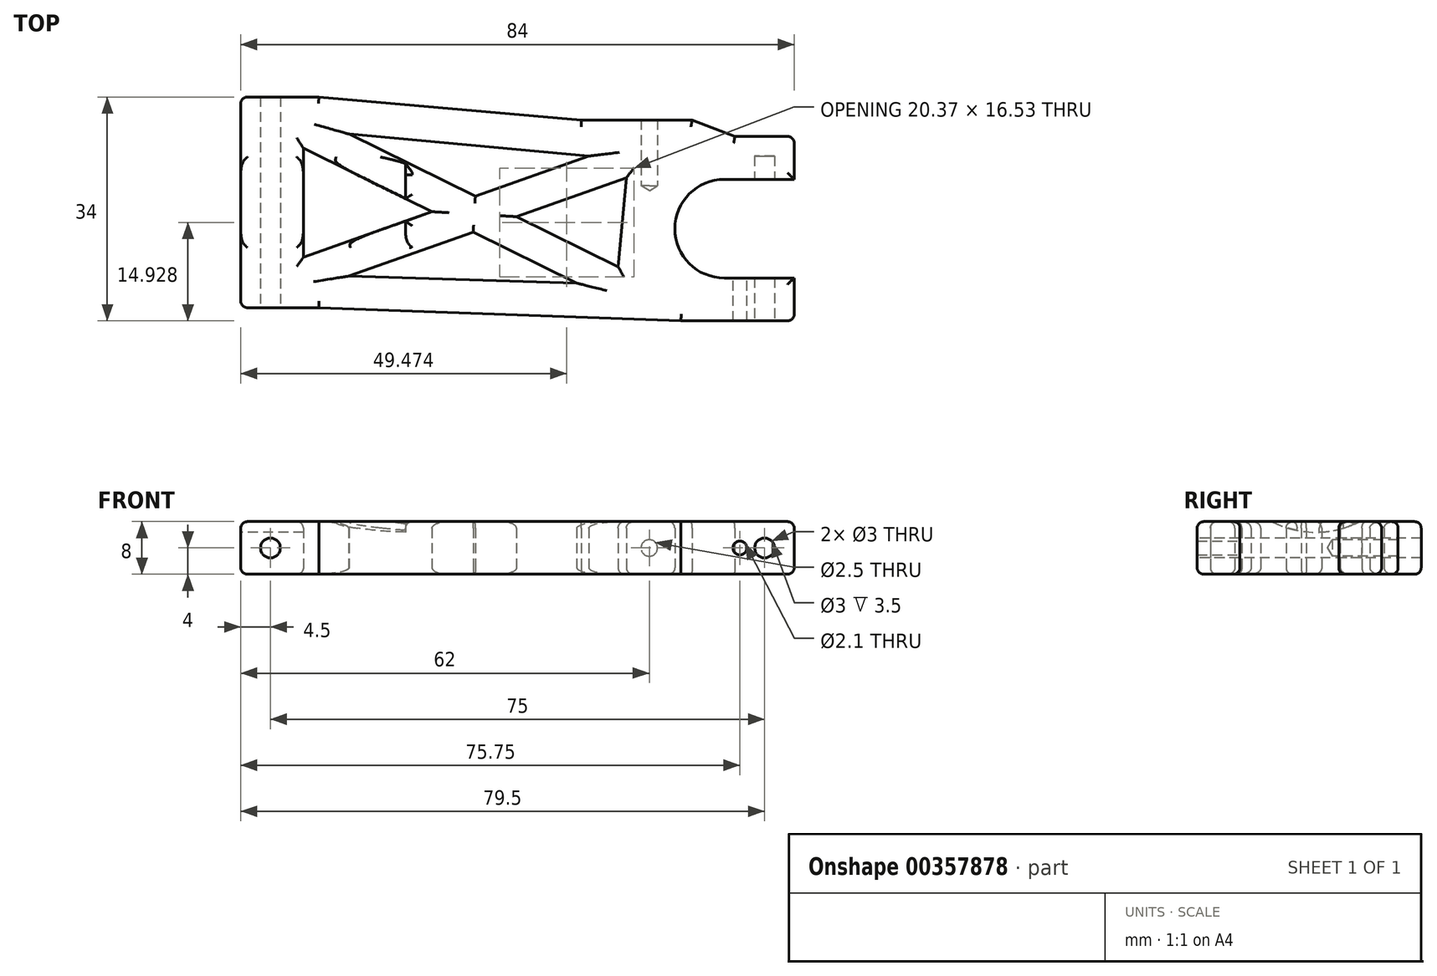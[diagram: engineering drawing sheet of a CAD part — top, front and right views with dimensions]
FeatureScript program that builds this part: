
annotation { "Feature Type Name" : "Feature", "Feature Type Description" : "" }
export const myFeature = defineFeature(function(context is Context, id is Id, definition is map)
    precondition{}
    {
        {
            var Q0;
            Q0=qCreatedBy(makeId("Top.planeOp"),FACE);
            var sketch = newSketch(context, id + "F0", { "sketchPlane" : qUnion([Q0])});
            skLineSegment(sketch, "E0", {"start": v(-37.5, 44.88) * mm, "end": v(-37.5, -3.08) * mm, "construction": true});
            skLineSegment(sketch, "E1", {"start": v(37.5, 44.88) * mm, "end": v(37.5, -31.83) * mm, "construction": true});
            skLineSegment(sketch, "E2", {"start": v(31.4, 0) * mm, "end": v(40.56, 0) * mm, "construction": true});
            skLineSegment(sketch, "E3", {"start": v(-41.87, 2) * mm, "end": v(-33.77, 2) * mm, "construction": true});
            skLineSegment(sketch, "E4", {"start": v(41.9, 28) * mm, "end": v(31.11, 28) * mm, "construction": true});
            skLineSegment(sketch, "E5", {"start": v(-40.76, 34) * mm, "end": v(-34.39, 34) * mm, "construction": true});
            skLineSegment(sketch, "E6", {"start": v(33.75, 2.56) * mm, "end": v(33.75, -2.35) * mm, "construction": true});
            skLineSegment(sketch, "E7", {"start": v(40.8, 30.5) * mm, "end": v(17.25, 30.5) * mm, "construction": true});
            skLineSegment(sketch, "E8", {"start": v(20, 32.37) * mm, "end": v(20, 27.7) * mm, "construction": true});
            skPoint(sketch, "E9", {"position": v(-37.5, 34) * mm});
            skPoint(sketch, "E10", {"position": v(-37.5, 2) * mm});
            skPoint(sketch, "E11", {"position": v(33.75, 0) * mm});
            skPoint(sketch, "E12", {"position": v(37.5, 0) * mm});
            skPoint(sketch, "E13", {"position": v(37.5, 28) * mm});
            skPoint(sketch, "E14", {"position": v(20, 30.5) * mm});
            skSolve(sketch);
        }
        {
            var Q0;
            Q0=qCreatedBy(makeId("Top.planeOp"),FACE);
            var sketch = newSketch(context, id + "F1", { "sketchPlane" : qUnion([Q0])});
            skLineSegment(sketch, "E15", {"start": v(-42, 34) * mm, "end": v(-42, 2) * mm});
            skLineSegment(sketch, "E16", {"start": v(-42, 2) * mm, "end": v(-30.15, 2) * mm});
            skLineSegment(sketch, "E17", {"start": v(-30.15, 2) * mm, "end": v(24.82, 0) * mm});
            skLineSegment(sketch, "E18", {"start": v(24.82, 0) * mm, "end": v(42, 0) * mm});
            skLineSegment(sketch, "E19", {"start": v(42, 0) * mm, "end": v(42, 28) * mm});
            skLineSegment(sketch, "E20", {"start": v(26.51, 30.5) * mm, "end": v(9.7, 30.5) * mm});
            skLineSegment(sketch, "E21", {"start": v(9.7, 30.5) * mm, "end": v(-30.15, 34) * mm});
            skLineSegment(sketch, "E22", {"start": v(-42, 34) * mm, "end": v(-30.15, 34) * mm});
            skLineSegment(sketch, "E23", {"start": v(42, 28) * mm, "end": v(33, 28) * mm});
            skLineSegment(sketch, "E24", {"start": v(33, 28) * mm, "end": v(26.51, 30.5) * mm});
            skLineSegment(sketch, "E25", {"start": v(-32.5, 29) * mm, "end": v(-32.5, 7) * mm});
            skLineSegment(sketch, "E26", {"start": v(32.5, 23.03) * mm, "end": v(32.5, 5) * mm});
            skLineSegment(sketch, "E27", {"start": v(-32.5, 29) * mm, "end": v(32.5, 23.03) * mm});
            skLineSegment(sketch, "E28", {"start": v(-32.5, 7) * mm, "end": v(32.5, 5) * mm});
            skPoint(sketch, "E29.startSnap0", {"position": v(-2.67, 1) * mm});
            skLineSegment(sketch, "E30", {"start": v(0, 6) * mm, "end": v(0, 26.01) * mm, "construction": true});
            skLineSegment(sketch, "E31", {"start": v(-32.5, 29) * mm, "end": v(15.03, 5.54) * mm, "construction": true});
            skLineSegment(sketch, "E32", {"start": v(-32.5, 7) * mm, "end": v(16.77, 24.47) * mm, "construction": true});
            skLineSegment(sketch, "E33", {"start": v(-6.56, 16.2) * mm, "end": v(15.37, 15.06) * mm, "construction": true});
            skLineSegment(sketch, "E34", {"start": v(15.37, 15.06) * mm, "end": v(32.5, 14.01) * mm, "construction": true});
            skLineSegment(sketch, "E35", {"start": v(-6.56, 16.2) * mm, "end": v(-32.5, 18) * mm, "construction": true});
            skLineSegment(sketch, "E36", {"start": v(-32.5, 26.21) * mm, "end": v(9.01, 5.72) * mm});
            skLineSegment(sketch, "E37", {"start": v(-25.56, 28.36) * mm, "end": v(21.06, 5.35) * mm});
            skLineSegment(sketch, "E38", {"start": v(-32.5, 9.65) * mm, "end": v(10.83, 25.02) * mm});
            skLineSegment(sketch, "E39", {"start": v(-25.62, 6.79) * mm, "end": v(22.72, 23.92) * mm});
            skPoint(sketch, "E40", {"position": v(42, 6.5) * mm});
            skPoint(sketch, "E41", {"position": v(42, 21.5) * mm});
            skLineSegment(sketch, "E42", {"start": v(42, 21.5) * mm, "end": v(31.38, 21.5) * mm});
            skLineSegment(sketch, "E43", {"start": v(42, 6.5) * mm, "end": v(31.38, 6.5) * mm});
            skArc(sketch, "E44", {"start": v(31.38, 21.5) * mm, "mid": v(23.88, 14) * mm, "end": v(31.38, 6.5) * mm});
            skLineSegment(sketch, "E45", {"start": v(15.03, 5.54) * mm, "end": v(16.77, 24.47) * mm});
            skSolve(sketch);
        }
        {
            var Q0;
            Q0=makeQuery(id+"F1.imprint","IMPRINT",FACE,{"disambiguationData":[TD([[makeQuery(id+"F1.imprint","IMPRINT",EDGE,{"derivedFrom":sQuery(id+"F1.wireOp",EDGE,"E15")}),1.0]])]});
            var Q1;
            {var subQ1=sQuery(id+"F1.wireOp",EDGE,"E27");var subQ6=sQuery(id+"F1.wireOp",EDGE,"E25");var subQ9=makeQuery(id+"F1.imprint","INTERSECT",VERTEX,{"derivedFrom":[subQ6,subQ1]});Q1=makeQuery(id+"F1.imprint","IMPRINT",FACE,{"disambiguationData":[TD([[makeQuery(id+"F1.imprint","IMPRINT",EDGE,{"disambiguationData":[TD([[subQ9,-1.0]])],"derivedFrom":subQ6}),1.0]])]});}
            var Q2;
            {var subQ0=sQuery(id+"F1.wireOp",EDGE,"E38");var subQ1=sQuery(id+"F1.wireOp",EDGE,"E36");var subQ2=makeQuery(id+"F1.imprint","INTERSECT",VERTEX,{"derivedFrom":[subQ1,subQ0]});Q2=makeQuery(id+"F1.imprint","IMPRINT",FACE,{"disambiguationData":[TD([[makeQuery(id+"F1.imprint","IMPRINT",EDGE,{"disambiguationData":[TD([[subQ2,-1.0]])],"derivedFrom":subQ1}),1.0]])]});}
            var Q3;
            {var subQ0=sQuery(id+"F1.wireOp",EDGE,"E38");var subQ1=sQuery(id+"F1.wireOp",EDGE,"E27");var subQ2=makeQuery(id+"F1.imprint","INTERSECT",VERTEX,{"derivedFrom":[subQ1,subQ0]});Q3=makeQuery(id+"F1.imprint","IMPRINT",FACE,{"disambiguationData":[TD([[makeQuery(id+"F1.imprint","IMPRINT",EDGE,{"disambiguationData":[TD([[subQ2,-1.0]])],"derivedFrom":subQ1}),-1.0]])]});}
            var Q4;
            {var subQ0=sQuery(id+"F1.wireOp",EDGE,"E39");var subQ1=sQuery(id+"F1.wireOp",EDGE,"E27");var subQ2=makeQuery(id+"F1.imprint","INTERSECT",VERTEX,{"derivedFrom":[subQ1,subQ0]});Q4=makeQuery(id+"F1.imprint","IMPRINT",FACE,{"disambiguationData":[TD([[makeQuery(id+"F1.imprint","IMPRINT",EDGE,{"disambiguationData":[TD([[subQ2,1.0]])],"derivedFrom":subQ1}),-1.0]])]});}
            var Q5;
            {var subQ16=sQuery(id+"F1.wireOp",EDGE,"E44");Q5=makeQuery(id+"F1.imprint","IMPRINT",FACE,{"disambiguationData":[TD([[makeQuery(id+"F1.imprint","IMPRINT",EDGE,{"derivedFrom":subQ16}),-1.0]])]});}
            var Q6;
            {var subQ0=sQuery(id+"F1.wireOp",EDGE,"E37");var subQ1=sQuery(id+"F1.wireOp",EDGE,"E28");var subQ2=makeQuery(id+"F1.imprint","INTERSECT",VERTEX,{"derivedFrom":[subQ1,subQ0]});Q6=makeQuery(id+"F1.imprint","IMPRINT",FACE,{"disambiguationData":[TD([[makeQuery(id+"F1.imprint","IMPRINT",EDGE,{"disambiguationData":[TD([[subQ2,1.0]])],"derivedFrom":subQ1}),1.0]])]});}
            var Q7;
            {var subQ1=sQuery(id+"F1.wireOp",EDGE,"E36");var subQ7=sQuery(id+"F1.wireOp",EDGE,"E28");var subQ8=makeQuery(id+"F1.imprint","INTERSECT",VERTEX,{"derivedFrom":[subQ7,subQ1]});Q7=makeQuery(id+"F1.imprint","IMPRINT",FACE,{"disambiguationData":[TD([[makeQuery(id+"F1.imprint","IMPRINT",EDGE,{"disambiguationData":[TD([[subQ8,-1.0]])],"derivedFrom":subQ7}),1.0]])]});}
            var Q8;
            {var subQ1=sQuery(id+"F1.wireOp",EDGE,"E25");var subQ5=sQuery(id+"F1.wireOp",EDGE,"E28");var subQ6=makeQuery(id+"F1.imprint","INTERSECT",VERTEX,{"derivedFrom":[subQ1,subQ5]});Q8=makeQuery(id+"F1.imprint","IMPRINT",FACE,{"disambiguationData":[TD([[makeQuery(id+"F1.imprint","IMPRINT",EDGE,{"disambiguationData":[TD([[subQ6,1.0]])],"derivedFrom":subQ1}),1.0]])]});}
            extrude(context, id + "F2", {"entities" : qUnion([Q0, Q1, Q2, Q3, Q4, Q5, Q6, Q7, Q8]), "depth" : 4 * mm});
        }
        {
            var Q0;
            Q0=makeQuery(id+"F2.opExtrude","CAP_FACE",FACE,{"disambiguationData":[OSD([sQuery(id+"F1.wireOp",EDGE,"E15"),sQuery(id+"F1.wireOp",EDGE,"E16"),sQuery(id+"F1.wireOp",EDGE,"E17"),sQuery(id+"F1.wireOp",EDGE,"E18"),sQuery(id+"F1.wireOp",EDGE,"E19"),sQuery(id+"F1.wireOp",EDGE,"E20"),sQuery(id+"F1.wireOp",EDGE,"E21"),sQuery(id+"F1.wireOp",EDGE,"E22"),sQuery(id+"F1.wireOp",EDGE,"E23"),sQuery(id+"F1.wireOp",EDGE,"E24"),sQuery(id+"F1.wireOp",EDGE,"E25"),sQuery(id+"F1.wireOp",EDGE,"E27"),sQuery(id+"F1.wireOp",EDGE,"E28"),sQuery(id+"F1.wireOp",EDGE,"E36"),sQuery(id+"F1.wireOp",EDGE,"E37"),sQuery(id+"F1.wireOp",EDGE,"E38"),sQuery(id+"F1.wireOp",EDGE,"E39"),sQuery(id+"F1.wireOp",EDGE,"E42"),sQuery(id+"F1.wireOp",EDGE,"E43"),sQuery(id+"F1.wireOp",EDGE,"E44"),sQuery(id+"F1.wireOp",EDGE,"E45")])],"isStart":true});
            extrude(context, id + "F3", {"entities" : qUnion([Q0]), "operationType" : NewBodyOperationType.ADD, "depth" : 4 * mm});
        }
        {
            var Q0;
            Q0=makeQuery(id+"F2.opExtrude","SWEPT_FACE",FACE,{"disambiguationData":[OSD([sQuery(id+"F1.wireOp",EDGE,"E22")])]});
            var sketch = newSketch(context, id + "F4", { "sketchPlane" : qUnion([Q0])});
            skPoint(sketch, "E46", {"position": v(37.5, 0) * mm});
            skSolve(sketch);
        }
        {
            var Q0;
            Q0=makeQuery(id+"F2.opExtrude","SWEPT_FACE",FACE,{"disambiguationData":[OSD([sQuery(id+"F1.wireOp",EDGE,"E18")])]});
            var sketch = newSketch(context, id + "F5", { "sketchPlane" : qUnion([Q0])});
            skPoint(sketch, "E47", {"position": v(33.75, 0) * mm});
            skPoint(sketch, "E48", {"position": v(37.5, 0) * mm});
            skCircle(sketch, "E49", {"center": v(37.5, 0) * mm, "radius": 1.5 * mm});
            skSolve(sketch);
        }
        {
            var Q0;
            Q0=sQuery(id+"F4.wireOp",VERTEX,"E46");
            var Q1;
            Q1=makeQuery(id+"F2.opExtrude","SWEPT_BODY",BODY,{"disambiguationData":[OSD([sQuery(id+"F1.wireOp",EDGE,"E15"),sQuery(id+"F1.wireOp",EDGE,"E16"),sQuery(id+"F1.wireOp",EDGE,"E17"),sQuery(id+"F1.wireOp",EDGE,"E18"),sQuery(id+"F1.wireOp",EDGE,"E19"),sQuery(id+"F1.wireOp",EDGE,"E20"),sQuery(id+"F1.wireOp",EDGE,"E21"),sQuery(id+"F1.wireOp",EDGE,"E22"),sQuery(id+"F1.wireOp",EDGE,"E23"),sQuery(id+"F1.wireOp",EDGE,"E24")])]});
            hole(context, id + "F6", {"style" : HoleStyle.SIMPLE, "endStyle" : HoleEndStyle.BLIND, "holeDiameter" : 3 * mm, "holeDepth" : 40 * mm, "isTappedThrough" : true, "tappedDepth" : 12 * mm, "tapClearance" : 3, "locations" : qUnion([Q0]), "scope" : qUnion([Q1])});
        }
        {
            var Q0;
            Q0=makeQuery(id+"F2.opExtrude","SWEPT_FACE",FACE,{"disambiguationData":[OSD([sQuery(id+"F1.wireOp",EDGE,"E20")])]});
            var sketch = newSketch(context, id + "F7", { "sketchPlane" : qUnion([Q0])});
            skPoint(sketch, "E50", {"position": v(-20, 0) * mm});
            skSolve(sketch);
        }
        {
            var Q0;
            Q0=sQuery(id+"F7.wireOp",VERTEX,"E50");
            var Q1;
            Q1=makeQuery(id+"F2.opExtrude","SWEPT_BODY",BODY,{"disambiguationData":[OSD([sQuery(id+"F1.wireOp",EDGE,"E15"),sQuery(id+"F1.wireOp",EDGE,"E16"),sQuery(id+"F1.wireOp",EDGE,"E17"),sQuery(id+"F1.wireOp",EDGE,"E18"),sQuery(id+"F1.wireOp",EDGE,"E19"),sQuery(id+"F1.wireOp",EDGE,"E20"),sQuery(id+"F1.wireOp",EDGE,"E21"),sQuery(id+"F1.wireOp",EDGE,"E22"),sQuery(id+"F1.wireOp",EDGE,"E23"),sQuery(id+"F1.wireOp",EDGE,"E24")])]});
            hole(context, id + "F8", {"style" : HoleStyle.SIMPLE, "endStyle" : HoleEndStyle.BLIND, "holeDiameter" : 2.5 * mm, "holeDepth" : 10 * mm, "isTappedThrough" : true, "tappedDepth" : 12 * mm, "tapClearance" : 3, "locations" : qUnion([Q0]), "scope" : qUnion([Q1])});
        }
        {
            var Q0;
            Q0=makeQuery(id+"F5.imprint","IMPRINT",FACE,{"disambiguationData":[TD([[makeQuery(id+"F5.imprint","IMPRINT",EDGE,{"derivedFrom":sQuery(id+"F5.wireOp",EDGE,"E49")}),1.0]])]});
            extrude(context, id + "F9", {"entities" : qUnion([Q0]), "operationType" : NewBodyOperationType.REMOVE, "oppositeDirection" : true, "depth" : 25 * mm});
        }
        {
            var Q0;
            {var subQ0=sQuery(id+"F1.wireOp",EDGE,"E15");Q0=makeQuery(id+"F3.boolean.opBoolean","MERGE",FACE,{"derivedFrom":[makeQuery(id+"F2.opExtrude","SWEPT_FACE",FACE,{"disambiguationData":[OSD([subQ0])]}),makeQuery(id+"F3.opExtrude","SWEPT_FACE",FACE,{"disambiguationData":[OSD([subQ0])]})]});}
            var sketch = newSketch(context, id + "F10", { "sketchPlane" : qUnion([Q0])});
            skArc(sketch, "E51", {"start": v(-24.65, 4) * mm, "mid": v(-18, 2.4) * mm, "end": v(-11.35, 4) * mm});
            skSolve(sketch);
        }
        {
            var Q0;
            {var subQ0=sQuery(id+"F10.wireOp",EDGE,"E51");Q0=makeQuery(id+"F10.imprint","IMPRINT",FACE,{"disambiguationData":[TD([[makeQuery(id+"F10.imprint","IMPRINT",EDGE,{"derivedFrom":subQ0}),1.0]])]});}
            extrude(context, id + "F11", {"entities" : qUnion([Q0]), "operationType" : NewBodyOperationType.REMOVE, "oppositeDirection" : true, "depth" : 25 * mm});
        }
        {
            var Q0;
            Q0=sQuery(id+"F5.wireOp",VERTEX,"E47");
            var Q1;
            Q1=makeQuery(id+"F2.opExtrude","SWEPT_BODY",BODY,{"disambiguationData":[OSD([sQuery(id+"F1.wireOp",EDGE,"E15"),sQuery(id+"F1.wireOp",EDGE,"E16"),sQuery(id+"F1.wireOp",EDGE,"E17"),sQuery(id+"F1.wireOp",EDGE,"E18"),sQuery(id+"F1.wireOp",EDGE,"E19"),sQuery(id+"F1.wireOp",EDGE,"E20"),sQuery(id+"F1.wireOp",EDGE,"E21"),sQuery(id+"F1.wireOp",EDGE,"E22"),sQuery(id+"F1.wireOp",EDGE,"E23"),sQuery(id+"F1.wireOp",EDGE,"E24")])]});
            hole(context, id + "F12", {"style" : HoleStyle.SIMPLE, "endStyle" : HoleEndStyle.BLIND, "holeDiameter" : 2.1 * mm, "holeDepth" : 10 * mm, "isTappedThrough" : true, "tappedDepth" : 12 * mm, "tapClearance" : 3, "locations" : qUnion([Q0]), "scope" : qUnion([Q1])});
        }
        {
            var Q0;
            Q0=makeQuery(id+"F3.opExtrude","CAP_FACE",FACE,{"disambiguationData":[OSD([sQuery(id+"F1.wireOp",EDGE,"E15"),sQuery(id+"F1.wireOp",EDGE,"E16"),sQuery(id+"F1.wireOp",EDGE,"E17"),sQuery(id+"F1.wireOp",EDGE,"E18"),sQuery(id+"F1.wireOp",EDGE,"E19"),sQuery(id+"F1.wireOp",EDGE,"E20"),sQuery(id+"F1.wireOp",EDGE,"E21"),sQuery(id+"F1.wireOp",EDGE,"E22"),sQuery(id+"F1.wireOp",EDGE,"E23"),sQuery(id+"F1.wireOp",EDGE,"E24"),sQuery(id+"F1.wireOp",EDGE,"E25"),sQuery(id+"F1.wireOp",EDGE,"E27"),sQuery(id+"F1.wireOp",EDGE,"E28"),sQuery(id+"F1.wireOp",EDGE,"E36"),sQuery(id+"F1.wireOp",EDGE,"E37"),sQuery(id+"F1.wireOp",EDGE,"E38"),sQuery(id+"F1.wireOp",EDGE,"E39"),sQuery(id+"F1.wireOp",EDGE,"E42"),sQuery(id+"F1.wireOp",EDGE,"E43"),sQuery(id+"F1.wireOp",EDGE,"E44"),sQuery(id+"F1.wireOp",EDGE,"E45")])],"isStart":false});
            var Q1;
            Q1=makeQuery(id+"F2.opExtrude","CAP_FACE",FACE,{"disambiguationData":[OSD([sQuery(id+"F1.wireOp",EDGE,"E15"),sQuery(id+"F1.wireOp",EDGE,"E16"),sQuery(id+"F1.wireOp",EDGE,"E17"),sQuery(id+"F1.wireOp",EDGE,"E18"),sQuery(id+"F1.wireOp",EDGE,"E19"),sQuery(id+"F1.wireOp",EDGE,"E20"),sQuery(id+"F1.wireOp",EDGE,"E21"),sQuery(id+"F1.wireOp",EDGE,"E22"),sQuery(id+"F1.wireOp",EDGE,"E23"),sQuery(id+"F1.wireOp",EDGE,"E24"),sQuery(id+"F1.wireOp",EDGE,"E25"),sQuery(id+"F1.wireOp",EDGE,"E27"),sQuery(id+"F1.wireOp",EDGE,"E28"),sQuery(id+"F1.wireOp",EDGE,"E36"),sQuery(id+"F1.wireOp",EDGE,"E37"),sQuery(id+"F1.wireOp",EDGE,"E38"),sQuery(id+"F1.wireOp",EDGE,"E39"),sQuery(id+"F1.wireOp",EDGE,"E42"),sQuery(id+"F1.wireOp",EDGE,"E43"),sQuery(id+"F1.wireOp",EDGE,"E44"),sQuery(id+"F1.wireOp",EDGE,"E45")])],"isStart":false});
            fillet(context, id + "F13", {"entities" : qUnion([Q0, Q1]), "radius" : 1 * mm, "tangentPropagation" : true, "allowEdgeOverflow" : false});
        }
        {
            var Q0;
            Q0=makeQuery(id+"F2.opExtrude","SWEPT_EDGE",EDGE,{"disambiguationData":[OSD([sQuery(id+"F1.wireOp",EDGE,"E15"),sQuery(id+"F1.wireOp",EDGE,"E16")])]});
            var Q1;
            Q1=makeQuery(id+"F2.opExtrude","SWEPT_EDGE",EDGE,{"disambiguationData":[OSD([sQuery(id+"F1.wireOp",EDGE,"E15"),sQuery(id+"F1.wireOp",EDGE,"E22")])]});
            var Q2;
            Q2=makeQuery(id+"F2.opExtrude","SWEPT_EDGE",EDGE,{"disambiguationData":[OSD([sQuery(id+"F1.wireOp",EDGE,"E18"),sQuery(id+"F1.wireOp",EDGE,"E19")])]});
            var Q3;
            Q3=makeQuery(id+"F2.opExtrude","SWEPT_EDGE",EDGE,{"disambiguationData":[OSD([sQuery(id+"F1.wireOp",EDGE,"E19"),sQuery(id+"F1.wireOp",EDGE,"E23")])]});
            fillet(context, id + "F14", {"entities" : qUnion([Q0, Q1, Q2, Q3]), "radius" : 1 * mm, "tangentPropagation" : true, "allowEdgeOverflow" : false});
        }
    });
